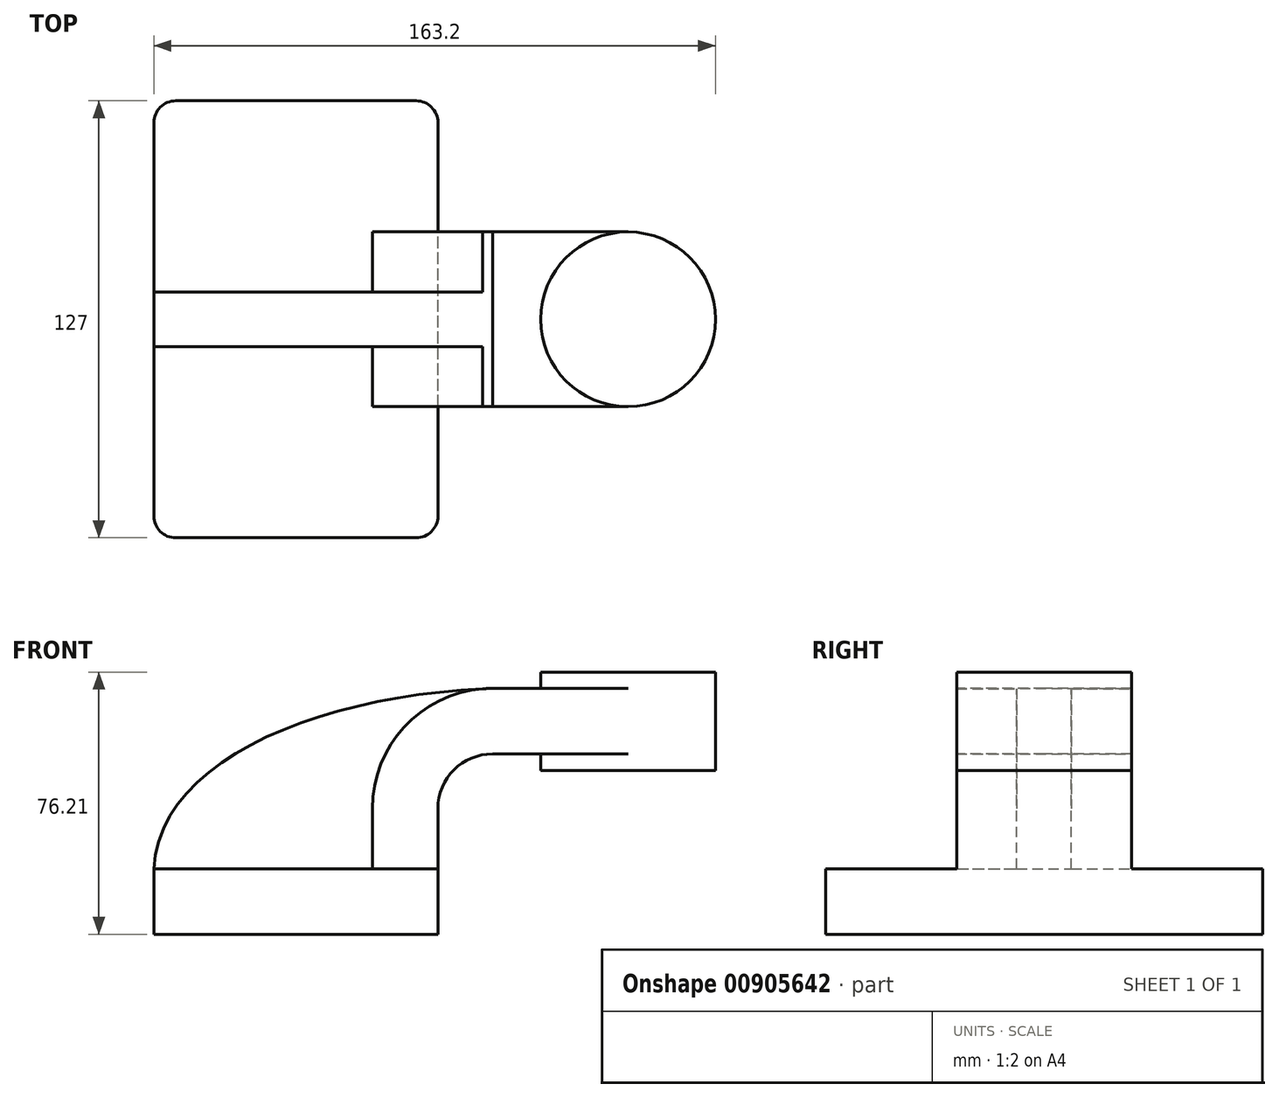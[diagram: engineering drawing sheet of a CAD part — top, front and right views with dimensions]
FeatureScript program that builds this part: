
annotation { "Feature Type Name" : "Feature", "Feature Type Description" : "" }
export const myFeature = defineFeature(function(context is Context, id is Id, definition is map)
    precondition{}
    {
        {
            var Q0;
            Q0=qCreatedBy(makeId("Front.planeOp"),FACE);
            var sketch = newSketch(context, id + "F0", { "sketchPlane" : qUnion([Q0])});
            skLineSegment(sketch, "E0.bottom", {"start": v(-41.28, 9.52) * mm, "end": v(41.28, 9.53) * mm});
            skLineSegment(sketch, "E0.top", {"start": v(-41.28, -9.53) * mm, "end": v(41.28, -9.53) * mm});
            skLineSegment(sketch, "E0.left", {"start": v(-41.28, 9.52) * mm, "end": v(-41.28, -9.53) * mm});
            skLineSegment(sketch, "E0.right", {"start": v(41.28, 9.53) * mm, "end": v(41.28, -9.52) * mm});
            skPoint(sketch, "E0.middle", {"position": v(0, 0) * mm});
            skLineSegment(sketch, "E1.bottom", {"start": v(71.12, 66.67) * mm, "end": v(121.92, 66.67) * mm});
            skLineSegment(sketch, "E1.top", {"start": v(71.12, 38.1) * mm, "end": v(121.92, 38.1) * mm});
            skLineSegment(sketch, "E1.left", {"start": v(71.12, 66.67) * mm, "end": v(71.12, 38.1) * mm});
            skLineSegment(sketch, "E1.right", {"start": v(121.92, 66.67) * mm, "end": v(121.92, 38.1) * mm});
            skPoint(sketch, "E1.middle", {"position": v(96.52, 52.39) * mm});
            skLineSegment(sketch, "E2", {"start": v(41.27, 9.53) * mm, "end": v(41.27, 27) * mm});
            skArc(sketch, "E3", {"start": v(41.27, 27) * mm, "mid": v(45.92, 38.23) * mm, "end": v(57.15, 42.88) * mm});
            skLineSegment(sketch, "E4", {"start": v(57.15, 42.88) * mm, "end": v(96.52, 42.88) * mm});
            skPoint(sketch, "E4.endSnap0", {"position": v(96.52, 38.1) * mm});
            skLineSegment(sketch, "E5.0", {"start": v(57.15, 61.93) * mm, "end": v(96.52, 61.93) * mm});
            skArc(sketch, "E5.1", {"start": v(22.22, 27) * mm, "mid": v(32.45, 51.7) * mm, "end": v(57.15, 61.93) * mm});
            skLineSegment(sketch, "E5.2", {"start": v(22.23, 9.53) * mm, "end": v(22.23, 27) * mm});
            skLineSegment(sketch, "E6", {"start": v(96.52, 38.1) * mm, "end": v(96.52, 66.67) * mm});
            skFitSpline(sketch, "E7", {"points": [v(-41.28, 9.53) * mm, v(57.15, 61.93) * mm], "startDerivative": vector(4.53, 96.62) * mm, "endDerivative": vector(146.57, 5.07) * mm});
            skSolve(sketch);
        }
        {
            var Q0;
            Q0=makeQuery(id+"F0.imprint","IMPRINT",FACE,{"disambiguationData":[TD([[makeQuery(id+"F0.imprint","IMPRINT",EDGE,{"derivedFrom":sQuery(id+"F0.wireOp",EDGE,"E0.top")}),1.0]])]});
            extrude(context, id + "F1", {"entities" : qUnion([Q0]), "endBound" : BoundingType.SYMMETRIC, "depth" : 127 * mm, "offsetDistance" : 25.4 * mm});
        }
        {
            var Q0;
            {var subQ1=sQuery(id+"F0.wireOp",EDGE,"E2");Q0=makeQuery(id+"F0.imprint","IMPRINT",FACE,{"disambiguationData":[TD([[makeQuery(id+"F0.imprint","IMPRINT",EDGE,{"derivedFrom":subQ1}),1.0]])]});}
            var Q1;
            {var subQ0=sQuery(id+"F0.wireOp",EDGE,"E5.0");var subQ1=sQuery(id+"F0.wireOp",EDGE,"E1.left");var subQ2=makeQuery(id+"F0.imprint","INTERSECT",VERTEX,{"derivedFrom":[subQ1,subQ0]});Q1=makeQuery(id+"F0.imprint","IMPRINT",FACE,{"disambiguationData":[TD([[makeQuery(id+"F0.imprint","IMPRINT",EDGE,{"disambiguationData":[TD([[subQ2,-1.0]])],"derivedFrom":subQ1}),1.0]])]});}
            extrude(context, id + "F2", {"entities" : qUnion([Q0, Q1]), "operationType" : NewBodyOperationType.ADD, "endBound" : BoundingType.SYMMETRIC, "depth" : 50.8 * mm, "offsetDistance" : 25.4 * mm});
        }
        {
            var Q0;
            {var subQ3=sQuery(id+"F0.wireOp",EDGE,"E5.2");Q0=makeQuery(id+"F0.imprint","IMPRINT",FACE,{"disambiguationData":[TD([[makeQuery(id+"F0.imprint","IMPRINT",EDGE,{"derivedFrom":subQ3}),1.0]])]});}
            extrude(context, id + "F3", {"entities" : qUnion([Q0]), "operationType" : NewBodyOperationType.ADD, "endBound" : BoundingType.SYMMETRIC, "depth" : 15.88 * mm, "offsetDistance" : 25.4 * mm});
        }
        {
            var Q0;
            {var subQ4=sQuery(id+"F0.wireOp",EDGE,"E1.right");Q0=makeQuery(id+"F0.imprint","IMPRINT",FACE,{"disambiguationData":[TD([[makeQuery(id+"F0.imprint","IMPRINT",EDGE,{"derivedFrom":subQ4}),-1.0]])]});}
            var Q1;
            Q1=sQuery(id+"F0.wireOp",EDGE,"E6");
            revolve(context, id + "F4", {"operationType" : NewBodyOperationType.ADD, "surfaceOperationType" : NewSurfaceOperationType.NEW, "entities" : qUnion([Q0]), "axis" : qUnion([Q1]), "revolveType" : RevolveType.FULL});
        }
        {
            var Q0;
            Q0=makeQuery(id+"F1.opExtrude","CAP_EDGE",EDGE,{"disambiguationData":[OSD([sQuery(id+"F0.wireOp",EDGE,"E0.right")])],"isStart":false});
            var Q1;
            Q1=makeQuery(id+"F1.opExtrude","CAP_EDGE",EDGE,{"disambiguationData":[OSD([sQuery(id+"F0.wireOp",EDGE,"E0.left")])],"isStart":false});
            var Q2;
            Q2=makeQuery(id+"F1.opExtrude","CAP_EDGE",EDGE,{"disambiguationData":[OSD([sQuery(id+"F0.wireOp",EDGE,"E0.right")])],"isStart":true});
            var Q3;
            Q3=makeQuery(id+"F1.opExtrude","CAP_EDGE",EDGE,{"disambiguationData":[OSD([sQuery(id+"F0.wireOp",EDGE,"E0.left")])],"isStart":true});
            fillet(context, id + "F5", {"entities" : qUnion([Q0, Q1, Q2, Q3]), "radius" : 6.35 * mm, "tangentPropagation" : true, "allowEdgeOverflow" : false});
        }
    });
